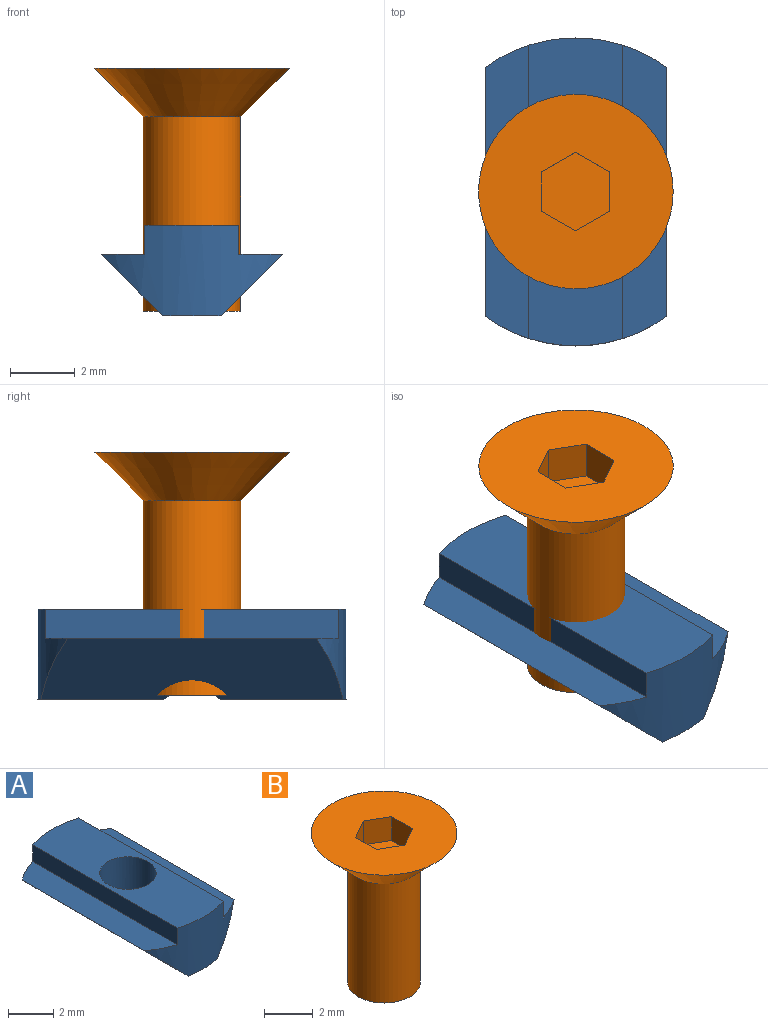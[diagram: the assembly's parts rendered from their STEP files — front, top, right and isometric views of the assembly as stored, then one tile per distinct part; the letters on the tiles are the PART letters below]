
ASSEMBLY  parts=2 mates=1
PART A: 12 faces, bbox 5.6x9.5x2.8 mm
  f0: plane 3.88x1.8mm, normal (0,0,-1), area 6.5mm2, adj f4,f6,f9,f11
  f1: plane 9.5x2.9mm, normal (0,0,1), area 22.2mm2, adj f2,f8,f9,f10,f11
  f2: plane 9.05x0.9mm, normal (-1,0,0), area 8.1mm2, adj f1,f3,f9,f10
  f3: plane 9.05x1.35mm, normal (0,0,1), area 11.4mm2, adj f2,f4,f9,f10
  f4: plane 9.33x1.9mm, normal (-0.71,0,-0.71), area 22.7mm2, adj f0,f3,f5,f9,f10,f11
  f5: plane 3.88x1.8mm, normal (0,0,-1), area 6.5mm2, adj f4,f6,f10,f11
  f6: plane 9.33x1.9mm, normal (0.71,0,-0.71), area 22.7mm2, adj f0,f5,f7,f9,f10,f11
  f7: plane 9.05x1.35mm, normal (0,0,1), area 11.4mm2, adj f6,f8,f9,f10
  f8: plane 9.05x0.9mm, normal (1,0,0), area 8.1mm2, adj f1,f7,f9,f10
  f9: cylinder r=4.75mm len=5.6mm, axis (0,0,1), area 9.9mm2, adj f0,f1,f2,f3,f4,f6,f7,f8
  f10: cylinder r=4.75mm len=5.6mm, axis (0,0,1), area 9.9mm2, adj f1,f2,f3,f4,f5,f6,f7,f8
  f11: cylinder r=1.25mm len=2.8mm, axis (0,0,1), area 21.1mm2, adj f0,f1,f4,f5,f6
PART B: 11 faces, bbox 6x6x7.5 mm
  f0: plane 6x6mm, normal (0,0,1), area 24.5mm2, adj f1,f4,f5,f6,f7,f8,f9
  f1: cone r=3mm half-angle=45deg, axis (0,0,1), area 30mm2, adj f0,f2
  f2: cylinder r=1.5mm len=6mm, axis (0,0,1), area 56.5mm2, adj f1,f3
  f3: plane 3x3mm, normal (0,0,-1), area 7.1mm2, adj f2
  f4: plane 1.21x1.2mm, normal (-1,0,0), area 1.5mm2, adj f0,f5,f9,f10
  f5: plane 1.2x1.05mm, normal (-0.5,-0.87,0), area 1.5mm2, adj f0,f4,f6,f10
  f6: plane 1.2x1.05mm, normal (0.5,-0.87,0), area 1.5mm2, adj f0,f5,f7,f10
  f7: plane 1.21x1.2mm, normal (1,0,0), area 1.5mm2, adj f0,f6,f8,f10
  f8: plane 1.2x1.05mm, normal (0.5,0.87,0), area 1.5mm2, adj f0,f7,f9,f10
  f9: plane 1.2x1.05mm, normal (-0.5,0.87,0), area 1.5mm2, adj f0,f4,f8,f10
  f10: plane 2.43x2.1mm, normal (0,0,1), area 3.8mm2, adj f4,f5,f6,f7,f8,f9
PLACE A at identity fixed
PLACE B t=(0,0,3.34)mm
MATE fastened B.f1 <-> A.f9  axis (0,0,1) through (0,0,3.34)mm
